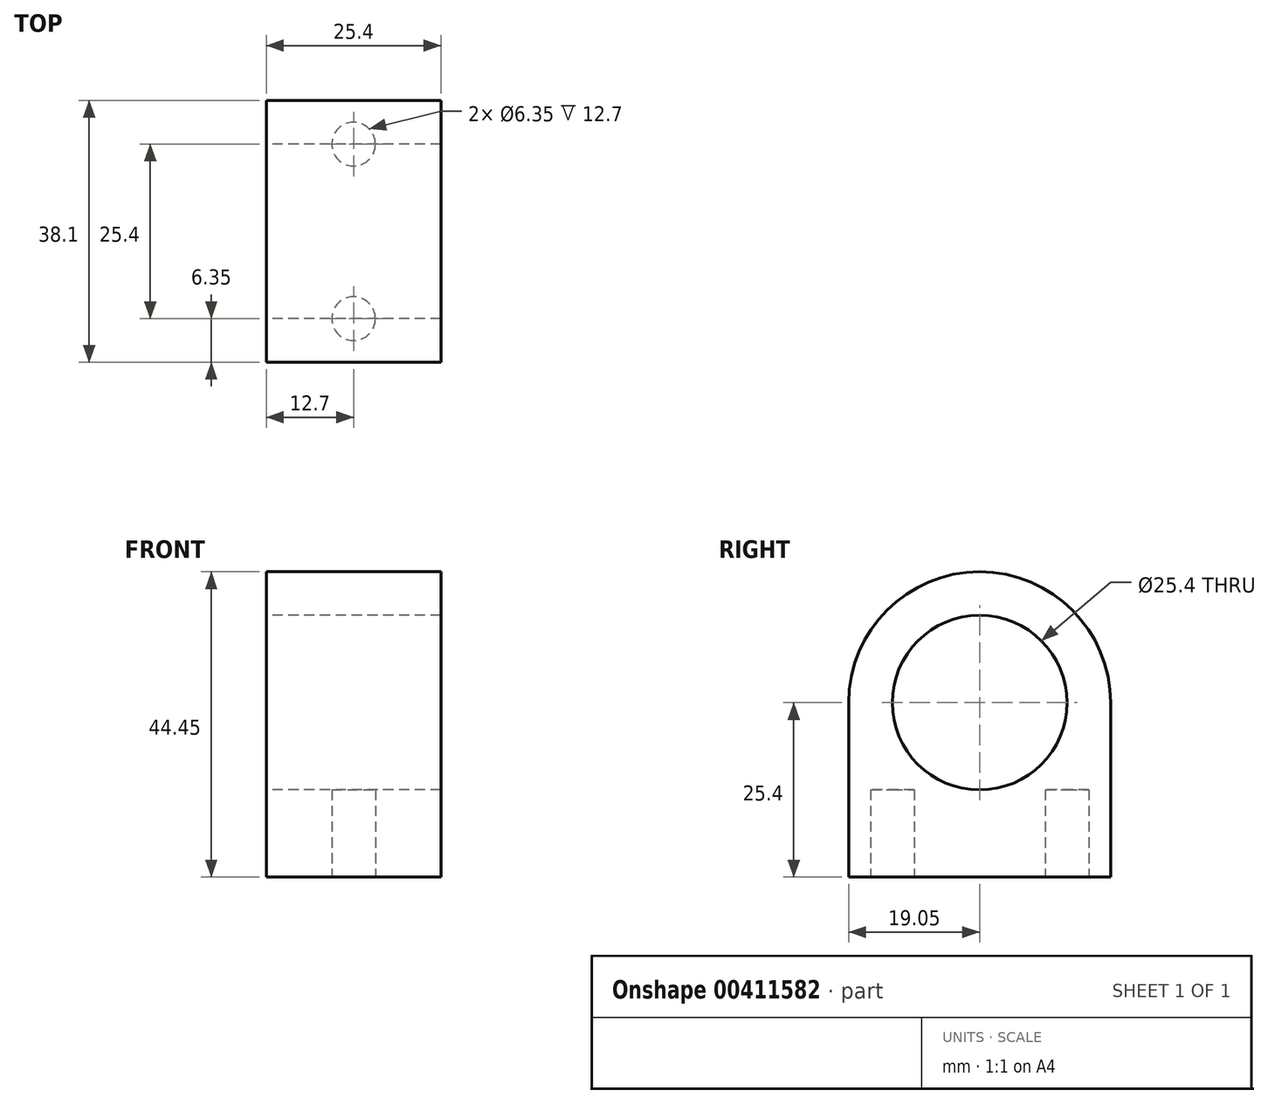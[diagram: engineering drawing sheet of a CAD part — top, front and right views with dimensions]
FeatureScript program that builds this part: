
annotation { "Feature Type Name" : "Feature", "Feature Type Description" : "" }
export const myFeature = defineFeature(function(context is Context, id is Id, definition is map)
    precondition{}
    {
        {
            var Q0;
            Q0=qCreatedBy(makeId("Right.planeOp"),FACE);
            var sketch = newSketch(context, id + "F0", { "sketchPlane" : qUnion([Q0])});
            skArc(sketch, "E0", {"start": v(19.05, 0) * mm, "mid": v(0, 19.05) * mm, "end": v(-19.05, 0) * mm});
            skLineSegment(sketch, "E1", {"start": v(-19.05, 0) * mm, "end": v(-19.05, -25.4) * mm});
            skLineSegment(sketch, "E2", {"start": v(-19.05, -25.4) * mm, "end": v(19.05, -25.4) * mm});
            skLineSegment(sketch, "E3", {"start": v(19.05, -25.4) * mm, "end": v(19.05, 0) * mm});
            skCircle(sketch, "E4", {"center": v(0, 0) * mm, "radius": 12.7 * mm});
            skSolve(sketch);
        }
        {
            var Q0;
            Q0 = qSketchRegion(id + "F0", true);
            extrude(context, id + "F1", {"entities" : qUnion([Q0]), "depth" : 25.4 * mm});
        }
        {
            var Q0;
            Q0=makeQuery(id+"F1.opExtrude","SWEPT_FACE",FACE,{"disambiguationData":[OSD([sQuery(id+"F0.wireOp",EDGE,"E2")])]});
            var sketch = newSketch(context, id + "F2", { "sketchPlane" : qUnion([Q0])});
            skCircle(sketch, "E5", {"center": v(12.7, 12.7) * mm, "radius": 3.18 * mm});
            skPoint(sketch, "E5.centerSnap0", {"position": v(12.7, 19.05) * mm});
            skCircle(sketch, "E6", {"center": v(12.7, -12.7) * mm, "radius": 3.18 * mm});
            skSolve(sketch);
        }
        {
            var Q0;
            Q0 = qSketchRegion(id + "F2", true);
            extrude(context, id + "F3", {"entities" : qUnion([Q0]), "operationType" : NewBodyOperationType.REMOVE, "oppositeDirection" : true, "depth" : 12.7 * mm});
        }
    });
